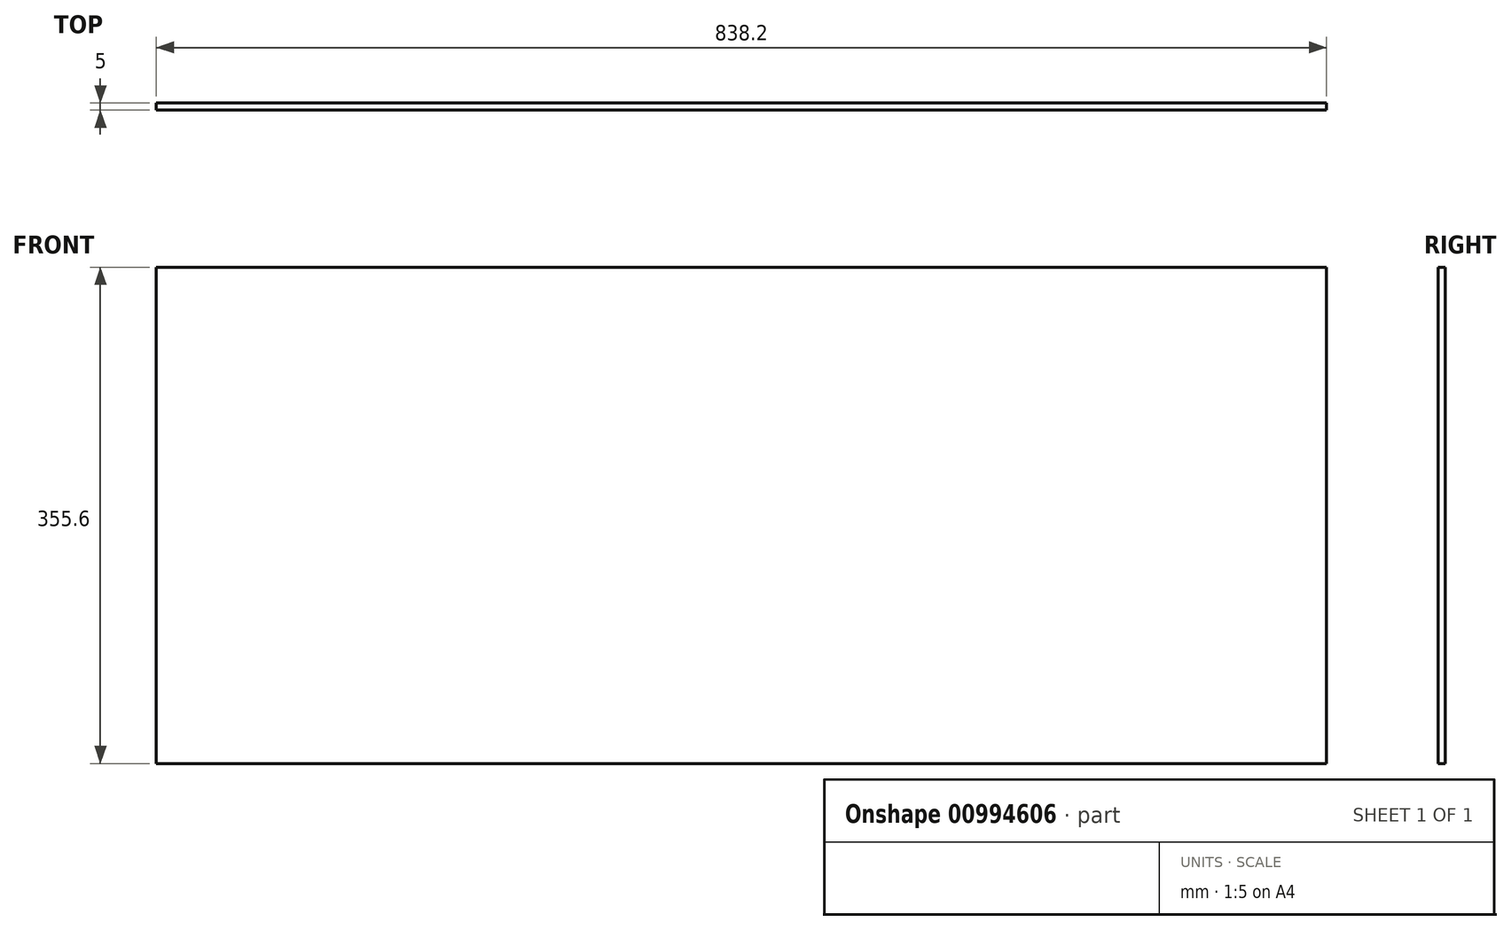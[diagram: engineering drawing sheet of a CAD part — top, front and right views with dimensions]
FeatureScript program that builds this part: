
annotation { "Feature Type Name" : "Feature", "Feature Type Description" : "" }
export const myFeature = defineFeature(function(context is Context, id is Id, definition is map)
    precondition{}
    {
        {
            var Q0;
            Q0=qCreatedBy(makeId("Front.planeOp"),FACE);
            var sketch = newSketch(context, id + "F0", { "sketchPlane" : qUnion([Q0])});
            skLineSegment(sketch, "E0.bottom", {"start": v(-419.1, -177.8) * mm, "end": v(419.1, -177.8) * mm});
            skLineSegment(sketch, "E0.top", {"start": v(-419.1, 177.8) * mm, "end": v(419.1, 177.8) * mm});
            skLineSegment(sketch, "E0.left", {"start": v(-419.1, -177.8) * mm, "end": v(-419.1, 177.8) * mm});
            skLineSegment(sketch, "E0.right", {"start": v(419.1, -177.8) * mm, "end": v(419.1, 177.8) * mm});
            skPoint(sketch, "E0.middle", {"position": v(0, 0) * mm});
            skSolve(sketch);
        }
        {
            var Q0;
            Q0=makeQuery(id+"F0.imprint","IMPRINT",FACE,{"disambiguationData":[TD([[makeQuery(id+"F0.imprint","IMPRINT",EDGE,{"derivedFrom":sQuery(id+"F0.wireOp",EDGE,"E0.bottom")}),1.0]])]});
            extrude(context, id + "F1", {"entities" : qUnion([Q0]), "depth" : 5 * mm, "offsetDistance" : 25 * mm});
        }
    });
